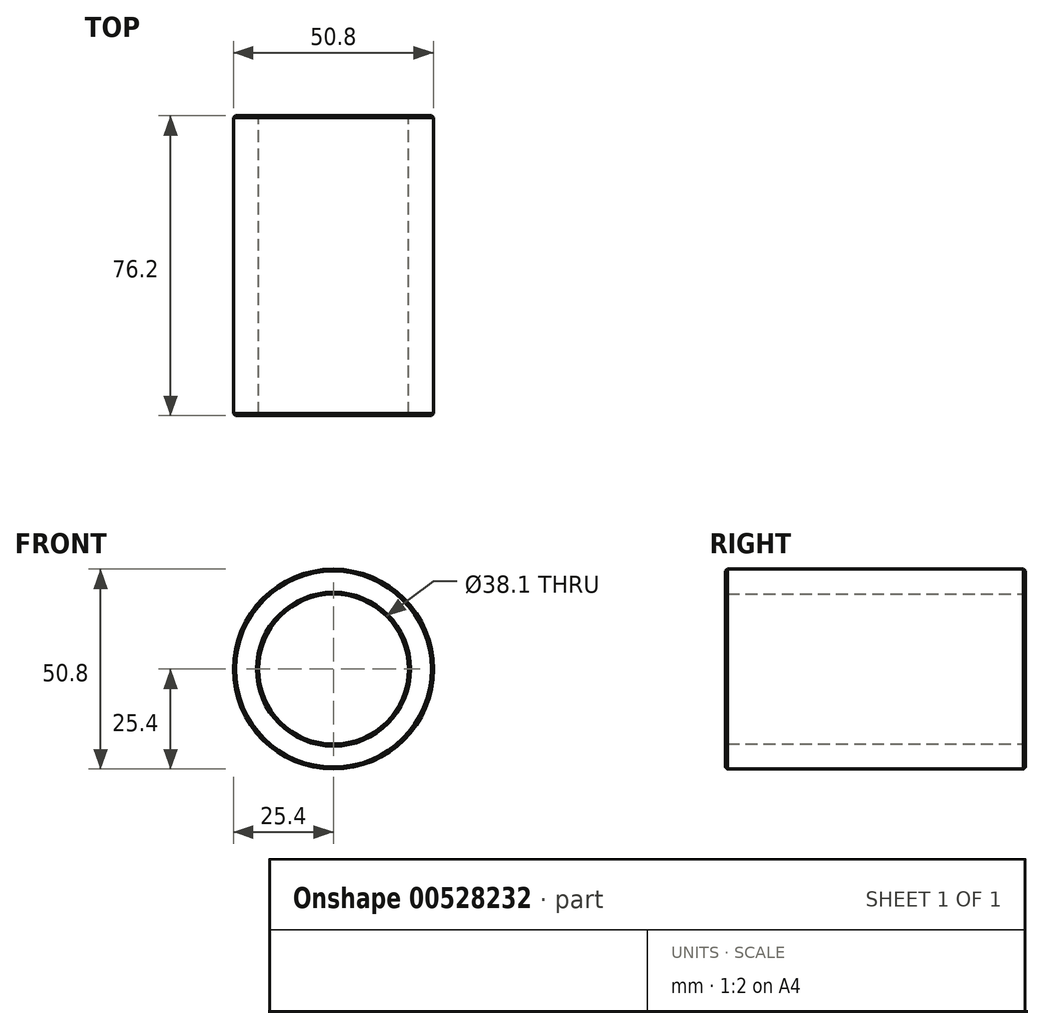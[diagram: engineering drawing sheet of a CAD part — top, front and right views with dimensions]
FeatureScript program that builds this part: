
annotation { "Feature Type Name" : "Feature", "Feature Type Description" : "" }
export const myFeature = defineFeature(function(context is Context, id is Id, definition is map)
    precondition{}
    {
        {
            var Q0;
            Q0=qCreatedBy(makeId("Front.planeOp"),FACE);
            var sketch = newSketch(context, id + "F0", { "sketchPlane" : qUnion([Q0])});
            skCircle(sketch, "E0", {"center": v(0, 0) * mm, "radius": 25.4 * mm});
            skCircle(sketch, "E1", {"center": v(0, 0) * mm, "radius": 19.05 * mm});
            skSolve(sketch);
        }
        {
            var Q0;
            Q0=makeQuery(id+"F0.imprint","IMPRINT",FACE,{"disambiguationData":[TD([[makeQuery(id+"F0.imprint","IMPRINT",EDGE,{"derivedFrom":sQuery(id+"F0.wireOp",EDGE,"E0")}),1.0]])]});
            extrude(context, id + "F1", {"entities" : qUnion([Q0]), "depth" : 76.2 * mm, "offsetDistance" : 25.4 * mm});
        }
        {
            var Q0;
            Q0=makeQuery(id+"F1.opExtrude","CAP_EDGE",EDGE,{"disambiguationData":[OSD([sQuery(id+"F0.wireOp",EDGE,"E0")])],"isStart":true});
            var Q1;
            Q1=makeQuery(id+"F1.opExtrude","CAP_EDGE",EDGE,{"disambiguationData":[OSD([sQuery(id+"F0.wireOp",EDGE,"E1")])],"isStart":true});
            var Q2;
            Q2=makeQuery(id+"F1.opExtrude","CAP_EDGE",EDGE,{"disambiguationData":[OSD([sQuery(id+"F0.wireOp",EDGE,"E1")])],"isStart":false});
            var Q3;
            Q3=makeQuery(id+"F1.opExtrude","CAP_EDGE",EDGE,{"disambiguationData":[OSD([sQuery(id+"F0.wireOp",EDGE,"E0")])],"isStart":false});
            chamfer(context, id + "F2", {"entities" : qUnion([Q0, Q1, Q2, Q3]), "width" : 0.5 * mm, "tangentPropagation" : true});
        }
    });
